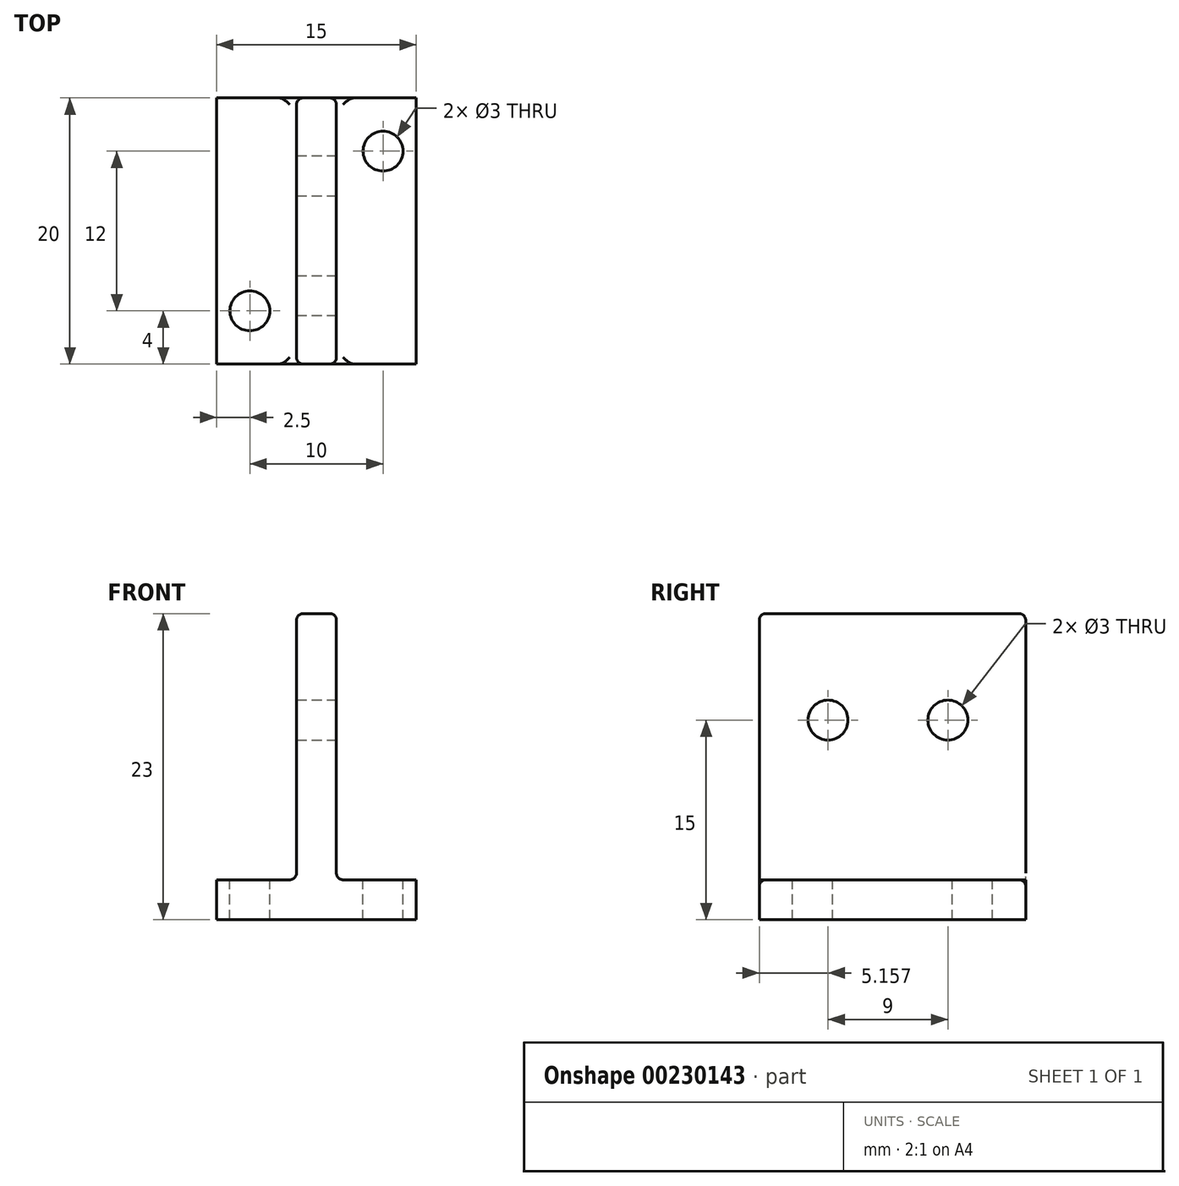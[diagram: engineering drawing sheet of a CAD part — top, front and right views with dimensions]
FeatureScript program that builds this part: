
annotation { "Feature Type Name" : "Feature", "Feature Type Description" : "" }
export const myFeature = defineFeature(function(context is Context, id is Id, definition is map)
    precondition{}
    {
        {
            var Q0;
            Q0=qCreatedBy(makeId("Front.planeOp"),FACE);
            var sketch = newSketch(context, id + "F0", { "sketchPlane" : qUnion([Q0])});
            skLineSegment(sketch, "E0.bottom", {"start": v(1.5, 10) * mm, "end": v(-1.5, 10) * mm});
            skLineSegment(sketch, "E0.top", {"start": v(1.5, -10) * mm, "end": v(-1.5, -10) * mm});
            skLineSegment(sketch, "E0.left", {"start": v(1.5, 10) * mm, "end": v(1.5, -10) * mm});
            skLineSegment(sketch, "E0.right", {"start": v(-1.5, 10) * mm, "end": v(-1.5, -10) * mm});
            skPoint(sketch, "E0.middle", {"position": v(0, 0) * mm});
            skPoint(sketch, "E1.middle", {"position": v(-1.5, -10) * mm});
            skLineSegment(sketch, "E2", {"start": v(-1.5, -10) * mm, "end": v(-7.5, -10) * mm});
            skLineSegment(sketch, "E3", {"start": v(-7.5, -10) * mm, "end": v(-7.5, -13) * mm});
            skLineSegment(sketch, "E4", {"start": v(-7.5, -13) * mm, "end": v(7.5, -13) * mm});
            skLineSegment(sketch, "E5", {"start": v(7.5, -13) * mm, "end": v(7.5, -10) * mm});
            skLineSegment(sketch, "E6", {"start": v(7.5, -10) * mm, "end": v(1.5, -10) * mm});
            skSolve(sketch);
        }
        {
            var Q0;
            Q0=makeQuery(id+"F0.imprint","IMPRINT",FACE,{"disambiguationData":[TD([[makeQuery(id+"F0.imprint","IMPRINT",EDGE,{"derivedFrom":sQuery(id+"F0.wireOp",EDGE,"E0.bottom")}),1.0]])]});
            var Q1;
            Q1=makeQuery(id+"F0.imprint","IMPRINT",FACE,{"disambiguationData":[TD([[makeQuery(id+"F0.imprint","IMPRINT",EDGE,{"derivedFrom":sQuery(id+"F0.wireOp",EDGE,"E0.top")}),1.0]])]});
            extrude(context, id + "F1", {"entities" : qUnion([Q0, Q1]), "depth" : 20 * mm});
        }
        {
            var Q0;
            Q0=makeQuery(id+"F1.opExtrude","SWEPT_FACE",FACE,{"disambiguationData":[OSD([sQuery(id+"F0.wireOp",EDGE,"E0.left")])]});
            var sketch = newSketch(context, id + "F2", { "sketchPlane" : qUnion([Q0])});
            skCircle(sketch, "E7", {"center": v(-14.84, 2) * mm, "radius": 1.5 * mm});
            skCircle(sketch, "E8", {"center": v(-5.84, 2) * mm, "radius": 1.5 * mm});
            skSolve(sketch);
        }
        {
            var Q0;
            Q0=makeQuery(id+"F2.imprint","IMPRINT",FACE,{"disambiguationData":[TD([[makeQuery(id+"F2.imprint","IMPRINT",EDGE,{"derivedFrom":sQuery(id+"F2.wireOp",EDGE,"E7")}),1.0]])]});
            var Q1;
            Q1=makeQuery(id+"F2.imprint","IMPRINT",FACE,{"disambiguationData":[TD([[makeQuery(id+"F2.imprint","IMPRINT",EDGE,{"derivedFrom":sQuery(id+"F2.wireOp",EDGE,"E8")}),1.0]])]});
            extrude(context, id + "F3", {"entities" : qUnion([Q0, Q1]), "operationType" : NewBodyOperationType.REMOVE, "endBound" : BoundingType.THROUGH_ALL, "oppositeDirection" : true, "depth" : 25 * mm});
        }
        {
            var Q0;
            Q0=makeQuery(id+"F1.opExtrude","SWEPT_FACE",FACE,{"disambiguationData":[OSD([sQuery(id+"F0.wireOp",EDGE,"E6")])]});
            var sketch = newSketch(context, id + "F4", { "sketchPlane" : qUnion([Q0])});
            skCircle(sketch, "E9", {"center": v(5, -4) * mm, "radius": 1.5 * mm});
            skSolve(sketch);
        }
        {
            var Q0;
            Q0=makeQuery(id+"F4.imprint","IMPRINT",FACE,{"disambiguationData":[TD([[makeQuery(id+"F4.imprint","IMPRINT",EDGE,{"derivedFrom":sQuery(id+"F4.wireOp",EDGE,"E9")}),1.0]])]});
            extrude(context, id + "F5", {"entities" : qUnion([Q0]), "operationType" : NewBodyOperationType.REMOVE, "endBound" : BoundingType.THROUGH_ALL, "oppositeDirection" : true, "depth" : 25 * mm});
        }
        {
            var Q0;
            Q0=makeQuery(id+"F1.opExtrude","SWEPT_FACE",FACE,{"disambiguationData":[OSD([sQuery(id+"F0.wireOp",EDGE,"E2")])]});
            var sketch = newSketch(context, id + "F6", { "sketchPlane" : qUnion([Q0])});
            skCircle(sketch, "E10", {"center": v(-5, -16) * mm, "radius": 1.5 * mm});
            skSolve(sketch);
        }
        {
            var Q0;
            Q0 = qSketchRegion(id + "F6", true);
            extrude(context, id + "F7", {"entities" : qUnion([Q0]), "operationType" : NewBodyOperationType.REMOVE, "oppositeDirection" : true, "depth" : 25 * mm});
        }
        {
            var Q0;
            Q0=makeQuery(id+"F1.opExtrude","SWEPT_EDGE",EDGE,{"disambiguationData":[OSD([sQuery(id+"F0.wireOp",EDGE,"E0.top"),sQuery(id+"F0.wireOp",EDGE,"E0.left"),sQuery(id+"F0.wireOp",EDGE,"E6")])]});
            var Q1;
            Q1=makeQuery(id+"F1.opExtrude","SWEPT_EDGE",EDGE,{"disambiguationData":[OSD([sQuery(id+"F0.wireOp",EDGE,"E0.top"),sQuery(id+"F0.wireOp",EDGE,"E0.right"),sQuery(id+"F0.wireOp",EDGE,"E2")])]});
            var Q2;
            Q2=makeQuery(id+"F1.opExtrude","SWEPT_EDGE",EDGE,{"disambiguationData":[OSD([sQuery(id+"F0.wireOp",EDGE,"E0.bottom"),sQuery(id+"F0.wireOp",EDGE,"E0.right")])]});
            var Q3;
            Q3=makeQuery(id+"F1.opExtrude","CAP_EDGE",EDGE,{"disambiguationData":[OSD([sQuery(id+"F0.wireOp",EDGE,"E0.left")])],"isStart":false});
            var Q4;
            Q4=makeQuery(id+"F1.opExtrude","CAP_EDGE",EDGE,{"disambiguationData":[OSD([sQuery(id+"F0.wireOp",EDGE,"E0.right")])],"isStart":false});
            var Q5;
            Q5=makeQuery(id+"F1.opExtrude","SWEPT_EDGE",EDGE,{"disambiguationData":[OSD([sQuery(id+"F0.wireOp",EDGE,"E0.bottom"),sQuery(id+"F0.wireOp",EDGE,"E0.left")])]});
            var Q6;
            Q6=makeQuery(id+"F1.opExtrude","CAP_EDGE",EDGE,{"disambiguationData":[OSD([sQuery(id+"F0.wireOp",EDGE,"E0.right")])],"isStart":true});
            var Q7;
            Q7=makeQuery(id+"F1.opExtrude","CAP_EDGE",EDGE,{"disambiguationData":[OSD([sQuery(id+"F0.wireOp",EDGE,"E0.left")])],"isStart":true});
            var Q8;
            Q8=makeQuery(id+"F1.opExtrude","CAP_EDGE",EDGE,{"disambiguationData":[OSD([sQuery(id+"F0.wireOp",EDGE,"E0.bottom")])],"isStart":false});
            var Q9;
            Q9=makeQuery(id+"F1.opExtrude","CAP_EDGE",EDGE,{"disambiguationData":[OSD([sQuery(id+"F0.wireOp",EDGE,"E0.bottom")])],"isStart":true});
            fillet(context, id + "F8", {"entities" : qUnion([Q0, Q1, Q2, Q3, Q4, Q5, Q6, Q7, Q8, Q9]), "radius" : .5 * mm, "tangentPropagation" : true, "allowEdgeOverflow" : false});
        }
    });
